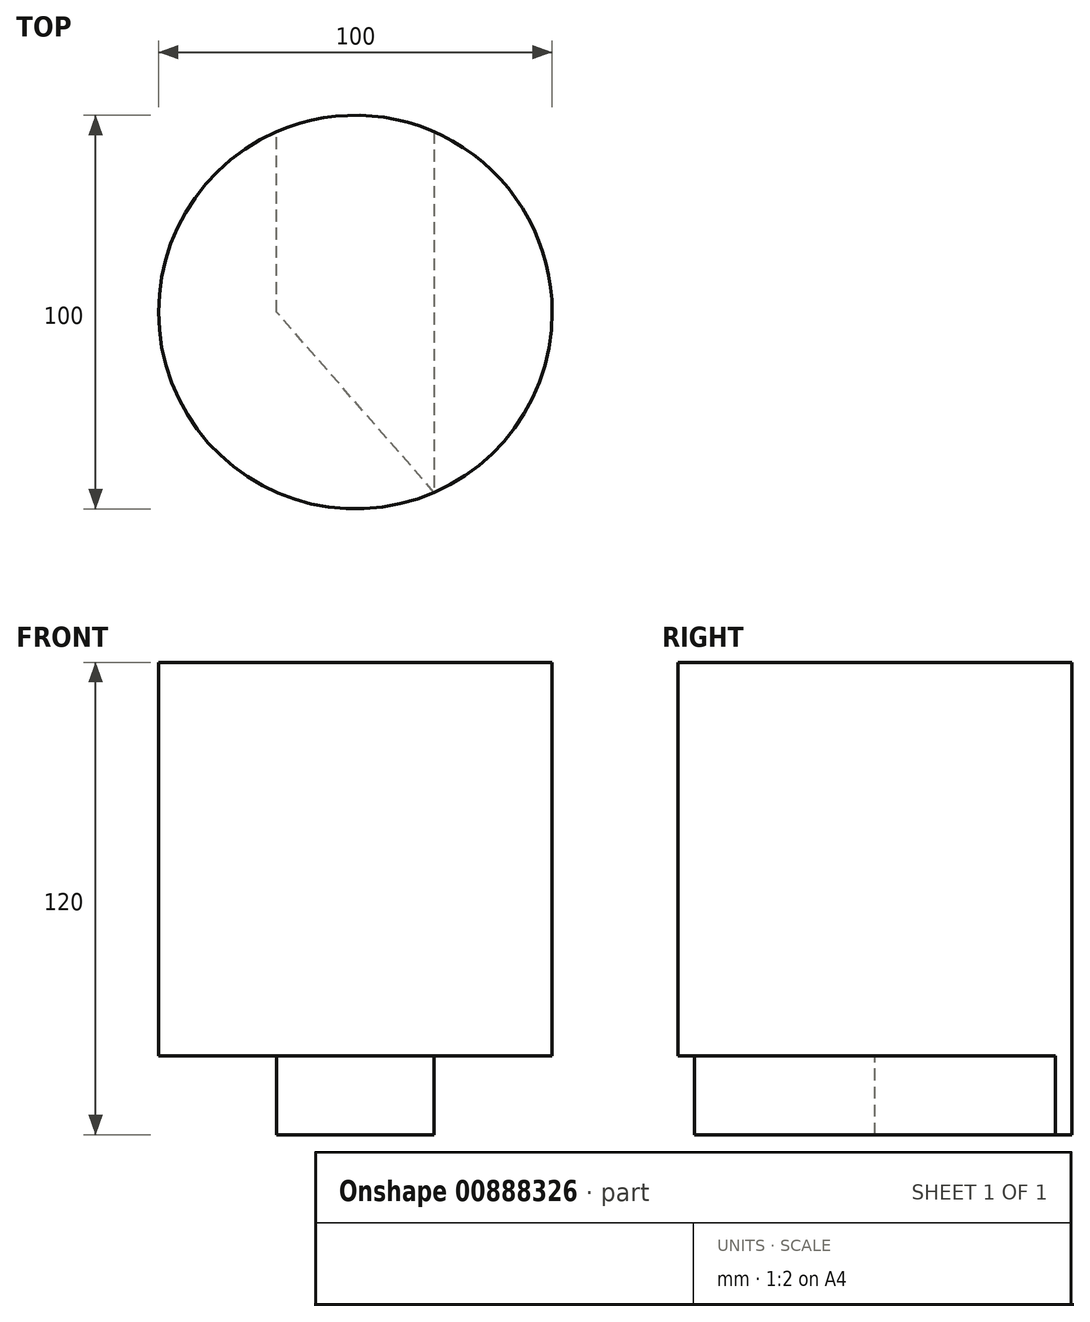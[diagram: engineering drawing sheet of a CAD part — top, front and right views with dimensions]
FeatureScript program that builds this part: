
annotation { "Feature Type Name" : "Feature", "Feature Type Description" : "" }
export const myFeature = defineFeature(function(context is Context, id is Id, definition is map)
    precondition{}
    {
        {
            var Q0;
            Q0=qCreatedBy(makeId("Top.planeOp"),FACE);
            var sketch = newSketch(context, id + "F0", { "sketchPlane" : qUnion([Q0])});
            skCircle(sketch, "E0", {"center": v(0, 0) * mm, "radius": 50 * mm});
            skSolve(sketch);
        }
        {
            var Q0;
            Q0 = qSketchRegion(id + "F0", true);
            extrude(context, id + "F1", {"entities" : qUnion([Q0]), "depth" : 100 * mm, "offsetDistance" : 25 * mm});
        }
        {
            var Q0;
            Q0=makeQuery(id+"F1.opExtrude","CAP_FACE",FACE,{"disambiguationData":[OSD([sQuery(id+"F0.wireOp",EDGE,"E0")])],"isStart":true});
            var sketch = newSketch(context, id + "F2", { "sketchPlane" : qUnion([Q0])});
            skLineSegment(sketch, "E1", {"start": v(0, 0) * mm, "end": v(20, 0) * mm});
            skLineSegment(sketch, "E2", {"start": v(20, 0) * mm, "end": v(-20, 0) * mm});
            skLineSegment(sketch, "E3", {"start": v(-20, 0) * mm, "end": v(-20, -45.83) * mm});
            skLineSegment(sketch, "E4", {"start": v(-20, -45.83) * mm, "end": v(20, -45.83) * mm});
            skLineSegment(sketch, "E5", {"start": v(20, -45.83) * mm, "end": v(20, 0) * mm});
            skLineSegment(sketch, "E6", {"start": v(20, 0) * mm, "end": v(20, 45.83) * mm});
            skLineSegment(sketch, "E7", {"start": v(20, 45.83) * mm, "end": v(-20, 0) * mm});
            skLineSegment(sketch, "E8", {"start": v(-20, 0) * mm, "end": v(20, 45.83) * mm});
            skLineSegment(sketch, "E9", {"start": v(20, 45.83) * mm, "end": v(1.78, 0) * mm});
            skLineSegment(sketch, "E10", {"start": v(-20, 0) * mm, "end": v(-20, 45.83) * mm});
            skSolve(sketch);
        }
        {
            var Q0;
            Q0 = qSketchRegion(id + "F2", true);
            var Q1;
            {var subQ0=sQuery(id+"F2.wireOp",EDGE,"E8");Q1=makeQuery(id+"F2.imprint","IMPRINT",FACE,{"disambiguationData":[TD([[makeQuery(id+"F2.imprint","IMPRINT",EDGE,{"derivedFrom":subQ0}),1.0]])]});}
            var Q2;
            {var subQ0=sQuery(id+"F2.wireOp",EDGE,"E4");Q2=makeQuery(id+"F2.imprint","IMPRINT",FACE,{"disambiguationData":[TD([[makeQuery(id+"F2.imprint","IMPRINT",EDGE,{"derivedFrom":subQ0}),-1.0]])]});}
            extrude(context, id + "F3", {"entities" : qUnion([Q0, Q1, Q2]), "operationType" : NewBodyOperationType.ADD, "depth" : 20 * mm, "offsetDistance" : 25 * mm});
        }
    });
